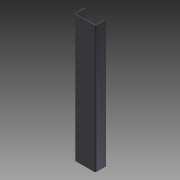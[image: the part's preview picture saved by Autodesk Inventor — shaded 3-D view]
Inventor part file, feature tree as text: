
AUTODESK INVENTOR PART (.ipt)
format: ipt  version: 2011 (Build 150239000, 239)  size: 89,600 bytes
history: native  units: mm (DEFAULTED — no unit token found)
features: extrude x1, shell x1, fillet x1, sketch x1
ambient origin geometry x8: Origin, YZ Plane, XZ Plane, XY Plane, X Axis, Y Axis, Z Axis, Center Point
bodies: Solid1 (feature_tree)
feature tree (4):
  extrude  "Extrusion1"  Depth=76.2mm
  shell  "Shell1"  Thickness=6.35mm
  fillet  "Fillet1"  Radius=0.381mm
  sketch  "Sketch1"  dims[d0=12.7mm d1=76.2mm d2=6.35mm d3=0.0mm d4=0.381mm d5=0.508mm d6=1.016mm]
